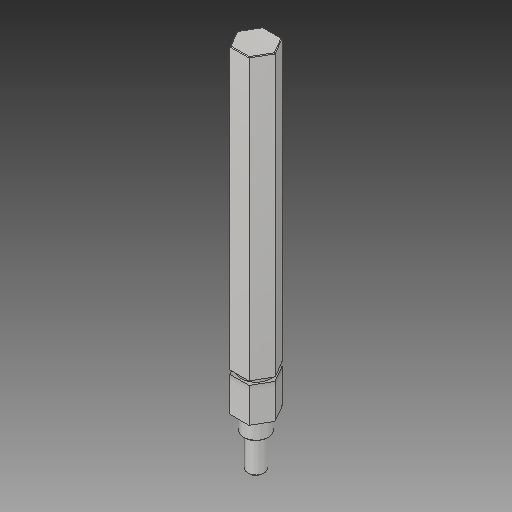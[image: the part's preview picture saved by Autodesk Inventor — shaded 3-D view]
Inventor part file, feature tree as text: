
AUTODESK INVENTOR PART (.ipt)
format: ipt  version: 2018 (Build 220112000, 112)  size: 116,736 bytes
history: native  units: in
note: dims shown in document units (in); Inventor stores cm internally (conversion verified against a paired STEP export)
features: chamfer x1
ambient origin geometry x8: Origin, YZ Plane, XZ Plane, XY Plane, X Axis, Y Axis, Z Axis, Center Point
bodies: Solid1 (feature_tree)
feature tree (1):
  chamfer  "Chamfer1"  [1 undecoded]
note: 1 required parameter value undecoded (feature->parameter linkage not recoverable at this tier; creation-order binding heuristic only, values carry confidence <= 0.55)
